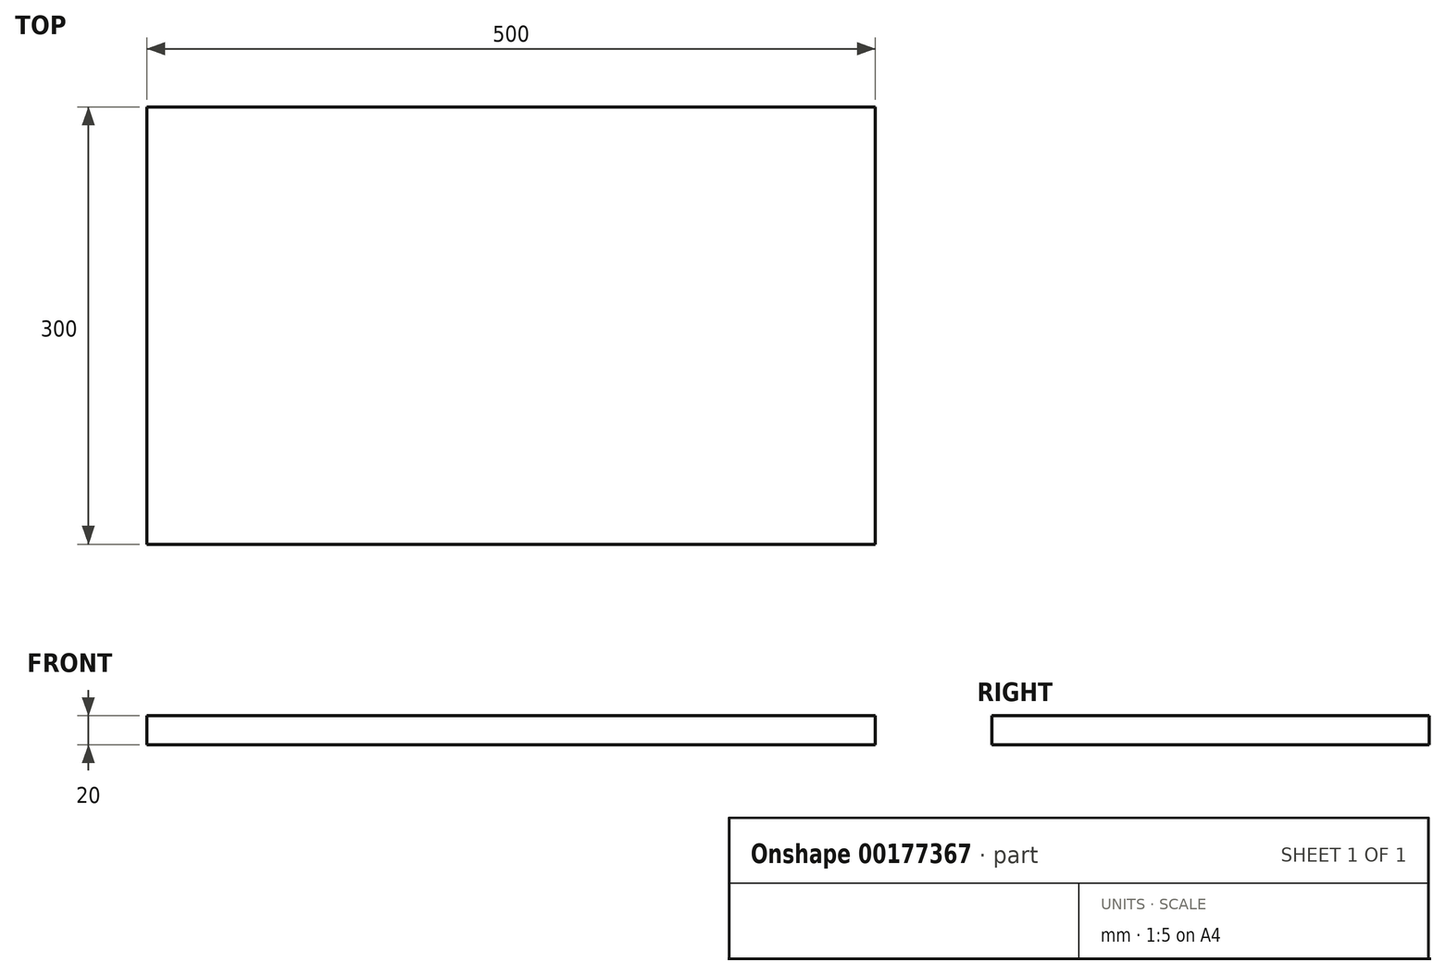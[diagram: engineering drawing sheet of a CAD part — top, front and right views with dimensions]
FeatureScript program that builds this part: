
annotation { "Feature Type Name" : "Feature", "Feature Type Description" : "" }
export const myFeature = defineFeature(function(context is Context, id is Id, definition is map)
    precondition{}
    {
        {
            var Q0;
            Q0=qCreatedBy(makeId("Front.planeOp"),FACE);
            var sketch = newSketch(context, id + "F0", { "sketchPlane" : qUnion([Q0])});
            skLineSegment(sketch, "E0", {"start": v(0, 0) * mm, "end": v(0, 20) * mm});
            skLineSegment(sketch, "E1", {"start": v(0, 20) * mm, "end": v(500, 20) * mm});
            skLineSegment(sketch, "E2", {"start": v(500, 20) * mm, "end": v(500, 0) * mm});
            skLineSegment(sketch, "E3", {"start": v(500, 0) * mm, "end": v(0, 0) * mm});
            skSolve(sketch);
        }
        {
            var Q0;
            Q0 = qSketchRegion(id + "F0", true);
            extrude(context, id + "F1", {"entities" : qUnion([Q0]), "depth" : 300 * mm, "offsetDistance" : 25 * mm});
        }
    });
